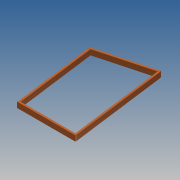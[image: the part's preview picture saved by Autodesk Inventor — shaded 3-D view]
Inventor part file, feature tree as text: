
AUTODESK INVENTOR PART (.ipt)
format: ipt  version: 2014 SP1 (Build 180222100, 222)  size: 113,152 bytes
history: native  units: in
note: dims shown in document units (in); Inventor stores cm internally (conversion verified against a paired STEP export)
features: extrude x3, sketch x3
ambient origin geometry x8: Origin, YZ Plane, XZ Plane, XY Plane, X Axis, Y Axis, Z Axis, Center Point
bodies: Solid1 (feature_tree)
feature tree (6):
  extrude  "Extrusion1"  Depth=0.5669in
  extrude  "Extrusion2"  TaperAngle=15.0deg  [1 undecoded]
  extrude  "Extrusion3"  Depth=1.4961in
  sketch  "Sketch1"  dims[d1=82.6772in d2=0.5669in]
  sketch  "Sketch2"  dims[d9=48.4252in d10=15.0deg]
  sketch  "Sketch3"  dims[d11=1.4961in d12=1.4961in d13=4.4882in d14=0.0in d15=0.0394in d16=0.0in d17=0.0394in d18=0.0in]
note: 1 required parameter value undecoded (feature->parameter linkage not recoverable at this tier; creation-order binding heuristic only, values carry confidence <= 0.55)
